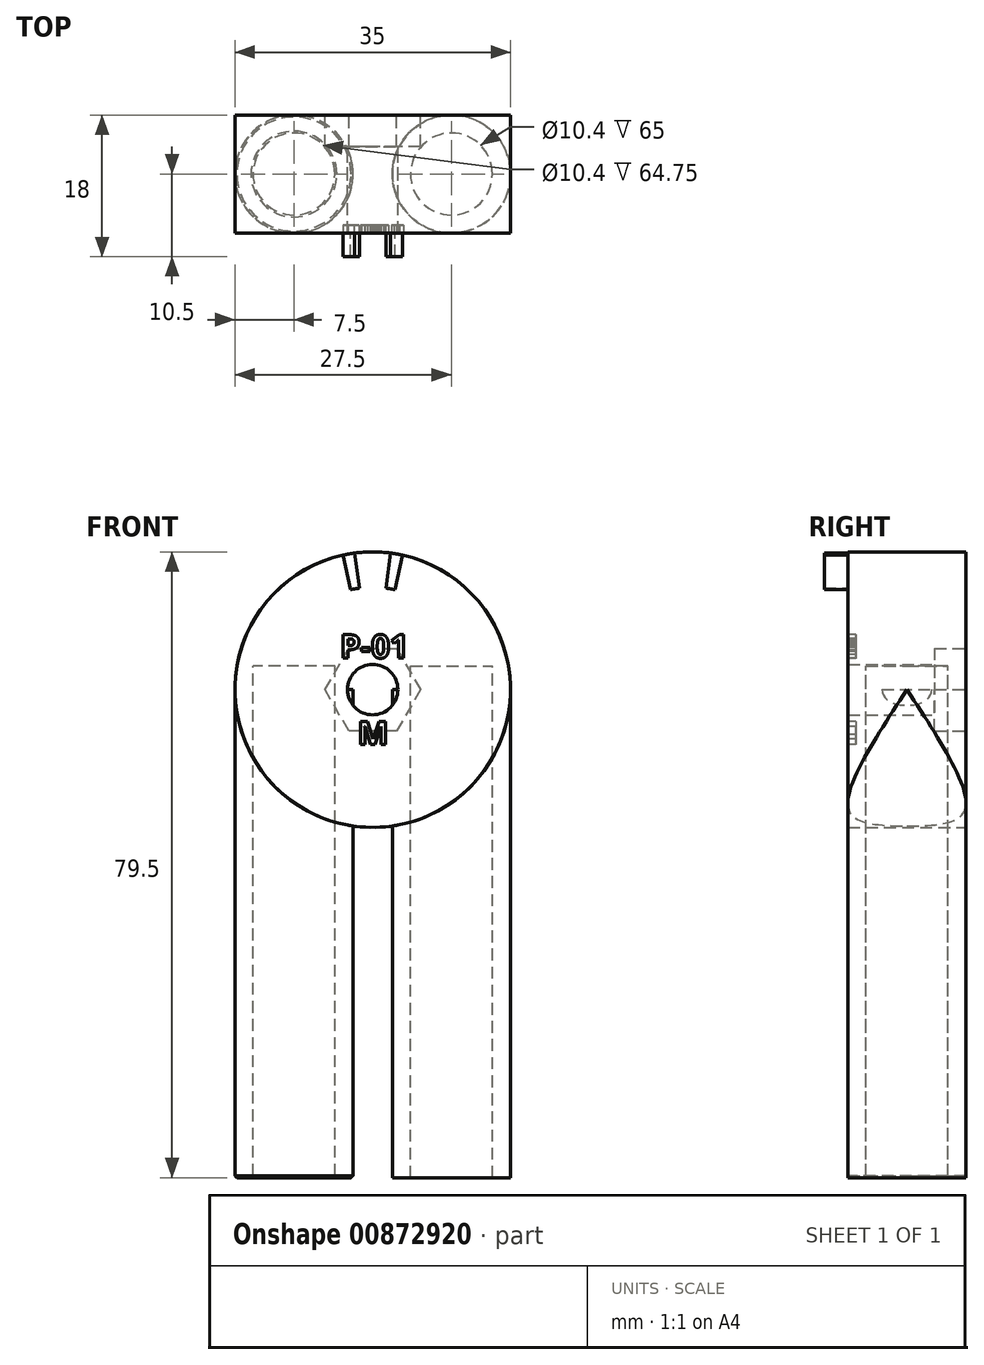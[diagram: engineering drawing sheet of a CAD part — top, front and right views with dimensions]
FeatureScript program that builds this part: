
annotation { "Feature Type Name" : "Feature", "Feature Type Description" : "" }
export const myFeature = defineFeature(function(context is Context, id is Id, definition is map)
    precondition{}
    {
        {
            var Q0;
            Q0=qCreatedBy(makeId("Front.planeOp"),FACE);
            var sketch = newSketch(context, id + "F0", { "sketchPlane" : qUnion([Q0])});
            skCircle(sketch, "E0", {"center": v(0, 0) * mm, "radius": 17.5 * mm});
            skCircle(sketch, "E1", {"center": v(0, 0) * mm, "radius": 3.2 * mm});
            skSolve(sketch);
        }
        {
            var Q0;
            Q0=qSketchRegion(id+"F0",true);
            extrude(context, id + "F1", {"entities" : qUnion([Q0]), "endBound" : BoundingType.SYMMETRIC, "depth" : 15 * mm, "offsetDistance" : 25 * mm});
        }
        {
            var Q0;
            Q0=makeQuery(id+"F1.opExtrude","CAP_FACE",FACE,{"disambiguationData":[OSD([sQuery(id+"F0.wireOp",EDGE,"E0")])],"isStart":false});
            var sketch = newSketch(context, id + "F2", { "sketchPlane" : qUnion([Q0])});
            skPoint(sketch, "E2.orphan", {"position": v(0, 0) * mm});
            skLineSegment(sketch, "E3", {"start": v(-42.27, 0) * mm, "end": v(49.07, 0) * mm, "construction": true});
            skLineSegment(sketch, "E4", {"start": v(0, -31.51) * mm, "end": v(0, 35.82) * mm, "construction": true});
            skArc(sketch, "E5", {"start": v(2.81, 12.7) * mm, "mid": v(2.26, 12.8) * mm, "end": v(1.7, 12.89) * mm});
            skArc(sketch, "E6", {"start": v(3.79, 17.09) * mm, "mid": v(3.04, 17.23) * mm, "end": v(2.28, 17.35) * mm});
            skLineSegment(sketch, "E7", {"start": v(1.7, 12.89) * mm, "end": v(2.28, 17.35) * mm});
            skLineSegment(sketch, "E8", {"start": v(3.79, 17.09) * mm, "end": v(2.81, 12.7) * mm});
            skLineSegment(sketch, "E9", {"start": v(0, 0) * mm, "end": v(3.04, 17.23) * mm, "construction": true});
            skSolve(sketch);
        }
        {
            var Q0;
            Q0=qSketchRegion(id+"F2",true);
            extrude(context, id + "F3", {"entities" : qUnion([Q0]), "operationType" : NewBodyOperationType.ADD, "depth" : 3 * mm, "offsetDistance" : 25 * mm});
        }
        {
            var Q0;
            Q0=qCreatedBy(makeId("Top.planeOp"),FACE);
            var sketch = newSketch(context, id + "F4", { "sketchPlane" : qUnion([Q0])});
            skCircle(sketch, "E10", {"center": v(-10, 0) * mm, "radius": 5.2 * mm});
            skCircle(sketch, "E11", {"center": v(-10, 0) * mm, "radius": 7.5 * mm, "construction": true});
            skSolve(sketch);
        }
        {
            var Q0;
            Q0=qSketchRegion(id+"F4",true);
            extrude(context, id + "F5", {"entities" : qUnion([Q0]), "operationType" : NewBodyOperationType.REMOVE, "oppositeDirection" : true, "depth" : 25 * mm, "offsetDistance" : 25 * mm, "hasSecondDirection" : true, "secondDirectionOppositeDirection" : false, "secondDirectionDepth" : 3 * mm});
        }
        {
            var Q0;
            Q0=qCreatedBy(makeId("Top.planeOp"),FACE);
            cPlane(context, id + "F6", {"entities" : qUnion([Q0]), "cplaneType" : CPlaneType.OFFSET, "offset" : 2 * mm, "oppositeDirection" : true, "width" : 150 * mm, "height" : 150 * mm});
        }
        {
            var Q0;
            Q0=qCreatedBy(id+"F6.planeOp",FACE);
            var sketch = newSketch(context, id + "F7", { "sketchPlane" : qUnion([Q0])});
            skCircle(sketch, "E12", {"center": v(-10, 0) * mm, "radius": 5.2 * mm});
            skCircle(sketch, "E13", {"center": v(-10, 0) * mm, "radius": 7.5 * mm});
            skSolve(sketch);
        }
        {
            var Q0;
            Q0=qSketchRegion(id+"F7",true);
            extrude(context, id + "F8", {"entities" : qUnion([Q0]), "operationType" : NewBodyOperationType.ADD, "oppositeDirection" : true, "depth" : 60 * mm, "offsetDistance" : 25 * mm, "hasSecondDirection" : true, "secondDirectionOppositeDirection" : false, "secondDirectionDepth" : 2 * mm});
        }
        {
            var Q0;
            Q0=makeQuery(id+"F1.opExtrude","CAP_FACE",FACE,{"disambiguationData":[OSD([sQuery(id+"F0.wireOp",EDGE,"E0"),sQuery(id+"F0.wireOp",EDGE,"E1")])],"isStart":true});
            var sketch = newSketch(context, id + "F9", { "sketchPlane" : qUnion([Q0])});
            skCircle(sketch, "E14.cCircle", {"center": v(0, 0) * mm, "radius": 6.06 * mm, "construction": true});
            skLineSegment(sketch, "E14.0", {"start": v(3.03, 5.25) * mm, "end": v(6.06, 0) * mm});
            skLineSegment(sketch, "E14.2", {"start": v(3.03, -5.25) * mm, "end": v(-3.03, -5.25) * mm});
            skLineSegment(sketch, "E14.3", {"start": v(-3.03, -5.25) * mm, "end": v(-6.06, 0) * mm});
            skLineSegment(sketch, "E14.4", {"start": v(-6.06, 0) * mm, "end": v(-3.03, 5.25) * mm});
            skLineSegment(sketch, "E14.5", {"start": v(-3.03, 5.25) * mm, "end": v(3.03, 5.25) * mm});
            skLineSegment(sketch, "E15", {"start": v(6.06, 0) * mm, "end": v(3.03, -5.25) * mm});
            skSolve(sketch);
        }
        {
            var Q0;
            Q0=qSketchRegion(id+"F9",true);
            extrude(context, id + "F10", {"entities" : qUnion([Q0]), "operationType" : NewBodyOperationType.REMOVE, "oppositeDirection" : true, "depth" : 4 * mm, "offsetDistance" : 25 * mm});
        }
        {
            var Q0;
            Q0=makeQuery(id+"F1.opExtrude","SWEPT_BODY",BODY,{"disambiguationData":[OSD([sQuery(id+"F0.wireOp",EDGE,"E0"),sQuery(id+"F0.wireOp",EDGE,"E1")])]});
            var Q1;
            Q1=qCreatedBy(makeId("Right.planeOp"),FACE);
            mirror(context, id + "F11", {"entities" : qUnion([Q0]), "mirrorPlane" : qUnion([Q1])});
        }
        {
            var Q0;
            Q0=makeQuery(id+"F1.opExtrude","CAP_FACE",FACE,{"disambiguationData":[OSD([sQuery(id+"F0.wireOp",EDGE,"E0"),sQuery(id+"F0.wireOp",EDGE,"E1")])],"isStart":false});
            var sketch = newSketch(context, id + "F12", { "sketchPlane" : qUnion([Q0])});
            skText(sketch, "E16", { "text": "P-01", "fontName": "OpenSans-Bold.ttf"});
            const initialGuessF12  = {"E16": [-0.00416, 0.004, 1, 0, 0.003]};
            skSetInitialGuess(sketch, initialGuessF12);
            skSolve(sketch);
        }
        {
            var Q0;
            Q0=qSketchRegion(id+"F12",true);
            extrude(context, id + "F13", {"entities" : qUnion([Q0]), "operationType" : NewBodyOperationType.REMOVE, "oppositeDirection" : true, "depth" : 1 * mm, "offsetDistance" : 25 * mm});
        }
        {
            var Q0;
            {var subQ1=sQuery(id+"F2.wireOp",EDGE,"E5");var subQ4=sQuery(id+"F0.wireOp",EDGE,"E0");var subQ5=sQuery(id+"F0.wireOp",EDGE,"E1");Q0=makeQuery(id+"F13.boolean.opBoolean","SPLIT",FACE,{"disambiguationData":[TD([makeQuery(id+"F11.opPattern","COPY",FACE,{"derivedFrom":makeQuery(id+"F3.opExtrude","SWEPT_FACE",FACE,{"disambiguationData":[OSD([subQ1])]}),"instanceName":"1"})])],"derivedFrom":makeQuery(id+"F11.opPattern","COPY",FACE,{"derivedFrom":makeQuery(id+"F1.opExtrude","CAP_FACE",FACE,{"disambiguationData":[OSD([subQ4,subQ5])],"isStart":false}),"instanceName":"1"})});}
            var sketch = newSketch(context, id + "F14", { "sketchPlane" : qUnion([Q0])});
            skText(sketch, "E17", { "text": "M", "fontName": "OpenSans-Bold.ttf"});
            const initialGuessF14  = {"E17": [-0.00191, -0.007, 1, 0, 0.003]};
            skSetInitialGuess(sketch, initialGuessF14);
            skSolve(sketch);
        }
        {
            var Q0;
            Q0=qSketchRegion(id+"F14",true);
            extrude(context, id + "F15", {"entities" : qUnion([Q0]), "operationType" : NewBodyOperationType.REMOVE, "oppositeDirection" : true, "depth" : 1 * mm, "offsetDistance" : 25 * mm});
        }
        {
            var Q0;
            Q0=makeQuery(id+"F8.opExtrude","CAP_FACE",FACE,{"disambiguationData":[OSD([sQuery(id+"F7.wireOp",EDGE,"E12"),sQuery(id+"F7.wireOp",EDGE,"E13")])],"isStart":false});
            chamfer(context, id + "F16", {"entities" : qUnion([Q0]), "width" : 0.25 * mm, "tangentPropagation" : true});
        }
    });
